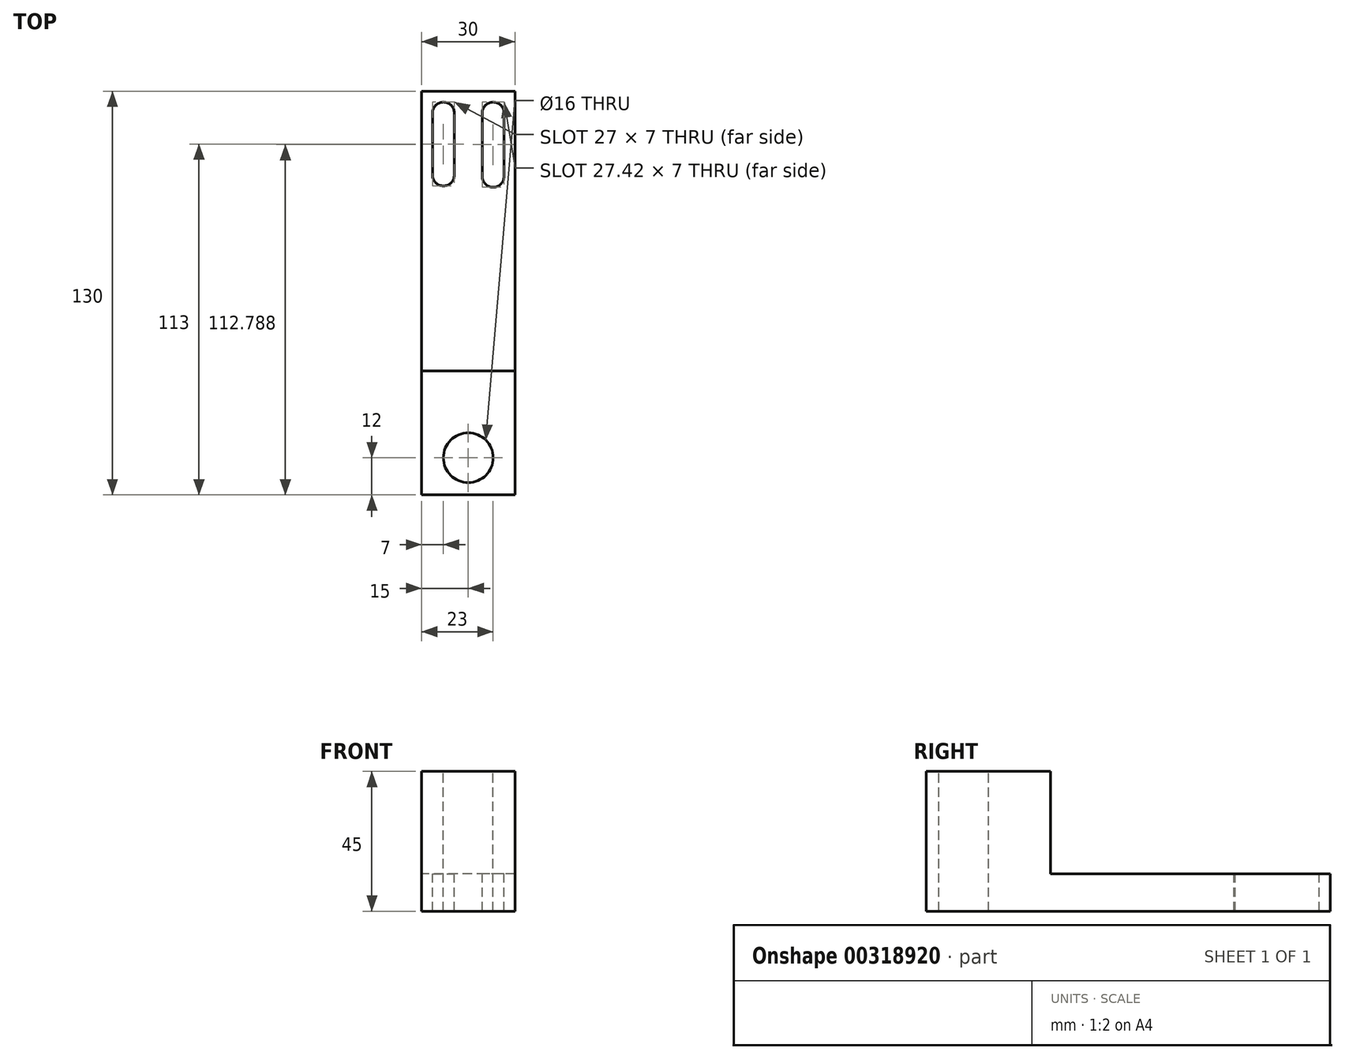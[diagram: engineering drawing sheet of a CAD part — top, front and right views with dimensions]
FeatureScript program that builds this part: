
annotation { "Feature Type Name" : "Feature", "Feature Type Description" : "" }
export const myFeature = defineFeature(function(context is Context, id is Id, definition is map)
    precondition{}
    {
        {
            var Q0;
            Q0=qCreatedBy(makeId("Right.planeOp"),FACE);
            var sketch = newSketch(context, id + "F0", { "sketchPlane" : qUnion([Q0])});
            skLineSegment(sketch, "E0.bottom", {"start": v(20, -22.5) * mm, "end": v(-20, -22.5) * mm});
            skLineSegment(sketch, "E0.top", {"start": v(20, 22.5) * mm, "end": v(-20, 22.5) * mm});
            skLineSegment(sketch, "E0.left", {"start": v(20, -10.5) * mm, "end": v(20, 22.5) * mm});
            skLineSegment(sketch, "E0.right", {"start": v(-20, -22.5) * mm, "end": v(-20, 22.5) * mm});
            skPoint(sketch, "E0.middle", {"position": v(0, 0) * mm});
            skLineSegment(sketch, "E1.bottom", {"start": v(20, -22.5) * mm, "end": v(110, -22.5) * mm});
            skLineSegment(sketch, "E1.top", {"start": v(20, -10.5) * mm, "end": v(110, -10.5) * mm});
            skLineSegment(sketch, "E1.right", {"start": v(110, -22.5) * mm, "end": v(110, -10.5) * mm});
            skSolve(sketch);
        }
        {
            var Q0;
            Q0=makeQuery(id+"F0.imprint","IMPRINT",FACE,{"disambiguationData":[TD([[makeQuery(id+"F0.imprint","IMPRINT",EDGE,{"derivedFrom":sQuery(id+"F0.wireOp",EDGE,"E0.bottom")}),-1.0]])]});
            extrude(context, id + "F1", {"entities" : qUnion([Q0]), "depth" : 30 * mm});
        }
        {
            var Q0;
            Q0=makeQuery(id+"F1.opExtrude","SWEPT_FACE",FACE,{"disambiguationData":[OSD([sQuery(id+"F0.wireOp",EDGE,"E1.top")])]});
            var sketch = newSketch(context, id + "F2", { "sketchPlane" : qUnion([Q0])});
            skLineSegment(sketch, "E2", {"start": v(3.5, 103) * mm, "end": v(3.5, 83) * mm});
            skLineSegment(sketch, "E3", {"start": v(26.5, 103) * mm, "end": v(26.5, 82.58) * mm});
            skLineSegment(sketch, "E4", {"start": v(19.5, 82.58) * mm, "end": v(19.5, 103) * mm});
            skLineSegment(sketch, "E5", {"start": v(10.5, 83) * mm, "end": v(10.5, 103) * mm});
            skArc(sketch, "E6", {"start": v(10.5, 103) * mm, "mid": v(7, 106.5) * mm, "end": v(3.5, 103) * mm});
            skArc(sketch, "E7", {"start": v(26.5, 103) * mm, "mid": v(23, 106.5) * mm, "end": v(19.5, 103) * mm});
            skArc(sketch, "E8", {"start": v(3.5, 83) * mm, "mid": v(7, 79.5) * mm, "end": v(10.5, 83) * mm});
            skArc(sketch, "E9", {"start": v(19.5, 82.58) * mm, "mid": v(23, 79.08) * mm, "end": v(26.5, 82.58) * mm});
            skSolve(sketch);
        }
        {
            var Q0;
            Q0=makeQuery(id+"F2.imprint","IMPRINT",FACE,{"disambiguationData":[TD([[makeQuery(id+"F2.imprint","IMPRINT",EDGE,{"derivedFrom":sQuery(id+"F2.wireOp",EDGE,"E2")}),1.0]])]});
            var Q1;
            Q1=makeQuery(id+"F2.imprint","IMPRINT",FACE,{"disambiguationData":[TD([[makeQuery(id+"F2.imprint","IMPRINT",EDGE,{"derivedFrom":sQuery(id+"F2.wireOp",EDGE,"E3")}),-1.0]])]});
            extrude(context, id + "F3", {"entities" : qUnion([Q0, Q1]), "operationType" : NewBodyOperationType.REMOVE, "oppositeDirection" : true, "depth" : 12 * mm});
        }
        {
            var Q0;
            Q0=makeQuery(id+"F1.opExtrude","SWEPT_FACE",FACE,{"disambiguationData":[OSD([sQuery(id+"F0.wireOp",EDGE,"E0.top")])]});
            var sketch = newSketch(context, id + "F4", { "sketchPlane" : qUnion([Q0])});
            skPoint(sketch, "E10.endSnap0", {"position": v(15, 20) * mm});
            skCircle(sketch, "E11", {"center": v(15, -8) * mm, "radius": 8 * mm});
            skSolve(sketch);
        }
        {
            var Q0;
            Q0=sQuery(id+"F4.wireOp",VERTEX,"E11.center");
            var Q1;
            Q1=makeQuery(id+"F1.opExtrude","SWEPT_BODY",BODY,{"disambiguationData":[OSD([sQuery(id+"F0.wireOp",EDGE,"E0.bottom"),sQuery(id+"F0.wireOp",EDGE,"E0.top"),sQuery(id+"F0.wireOp",EDGE,"E0.left"),sQuery(id+"F0.wireOp",EDGE,"E0.right"),sQuery(id+"F0.wireOp",EDGE,"E1.bottom"),sQuery(id+"F0.wireOp",EDGE,"E1.top"),sQuery(id+"F0.wireOp",EDGE,"E1.right")])]});
            hole(context, id + "F5", {"style" : HoleStyle.SIMPLE, "endStyle" : HoleEndStyle.THROUGH, "holeDiameter" : 16 * mm, "tappedDepth" : 12 * mm, "tapClearance" : 3, "startFromSketch" : true, "locations" : qUnion([Q0]), "scope" : qUnion([Q1])});
        }
    });
